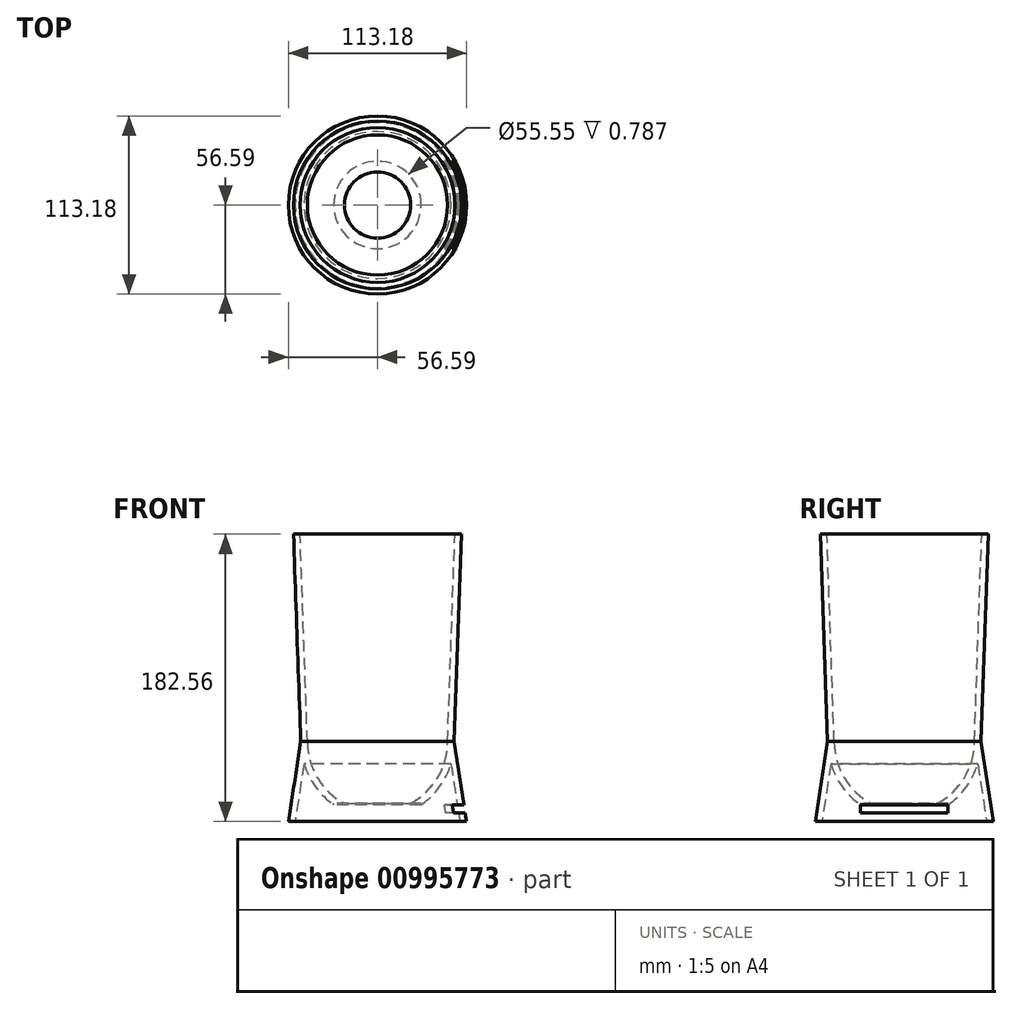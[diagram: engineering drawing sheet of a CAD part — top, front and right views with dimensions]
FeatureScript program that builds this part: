
annotation { "Feature Type Name" : "Feature", "Feature Type Description" : "" }
export const myFeature = defineFeature(function(context is Context, id is Id, definition is map)
    precondition{}
    {
        {
            var Q0;
            Q0=qCreatedBy(makeId("Front.planeOp"),FACE);
            var sketch = newSketch(context, id + "F0", { "sketchPlane" : qUnion([Q0])});
            skLineSegment(sketch, "E0", {"start": v(0, 0) * mm, "end": v(48.74, 0) * mm});
            skLineSegment(sketch, "E1", {"start": v(48.74, 0) * mm, "end": v(56.6, -50.8) * mm});
            skLineSegment(sketch, "E2", {"start": v(56.6, -50.8) * mm, "end": v(0, -50.8) * mm});
            skLineSegment(sketch, "E3", {"start": v(0, -50.8) * mm, "end": v(0, 0) * mm});
            skSolve(sketch);
        }
        {
            var Q0;
            Q0=makeQuery(id+"F0.imprint","IMPRINT",FACE,{"disambiguationData":[TD([[makeQuery(id+"F0.imprint","IMPRINT",EDGE,{"derivedFrom":sQuery(id+"F0.wireOp",EDGE,"E0")}),-1.0]])]});
            var Q1;
            Q1=sQuery(id+"F0.wireOp",EDGE,"E3");
            revolve(context, id + "F1", {"surfaceOperationType" : NewSurfaceOperationType.NEW, "entities" : qUnion([Q0]), "axis" : qUnion([Q1]), "revolveType" : RevolveType.FULL});
        }
        {
            var Q0;
            Q0=qCreatedBy(makeId("Front.planeOp"),FACE);
            var sketch = newSketch(context, id + "F2", { "sketchPlane" : qUnion([Q0])});
            skLineSegment(sketch, "E4.0", {"start": v(48.74, 0) * mm, "end": v(-48.74, 0) * mm, "construction": true});
            skLineSegment(sketch, "E5", {"start": v(0, 0) * mm, "end": v(48.74, 0) * mm});
            skLineSegment(sketch, "E6", {"start": v(0, 0) * mm, "end": v(0, 131.76) * mm});
            skLineSegment(sketch, "E7", {"start": v(0, 131.76) * mm, "end": v(53.34, 131.76) * mm});
            skLineSegment(sketch, "E8", {"start": v(53.34, 131.76) * mm, "end": v(48.74, 0) * mm});
            skSolve(sketch);
        }
        {
            var Q0;
            Q0=makeQuery(id+"F2.imprint","IMPRINT",FACE,{"disambiguationData":[TD([[makeQuery(id+"F2.imprint","IMPRINT",EDGE,{"derivedFrom":sQuery(id+"F2.wireOp",EDGE,"E5")}),1.0]])]});
            var Q1;
            Q1=sQuery(id+"F2.wireOp",EDGE,"E6");
            revolve(context, id + "F3", {"operationType" : NewBodyOperationType.ADD, "surfaceOperationType" : NewSurfaceOperationType.NEW, "entities" : qUnion([Q0]), "axis" : qUnion([Q1]), "revolveType" : RevolveType.FULL});
        }
        {
            var Q0;
            Q0=makeQuery(id+"F3.opRevolve","SWEPT_FACE",FACE,{"disambiguationData":[OSD([sQuery(id+"F2.wireOp",EDGE,"E7")])]});
            var Q1;
            Q1=makeQuery(id+"F1.opRevolve","SWEPT_FACE",FACE,{"disambiguationData":[OSD([sQuery(id+"F0.wireOp",EDGE,"E2")])]});
            shell(context, id + "F4", {"entities" : qUnion([Q0, Q1]), "thickness" : 4.2 * mm});
        }
        {
            var Q0;
            Q0=qCreatedBy(makeId("Right.planeOp"),FACE);
            var sketch = newSketch(context, id + "F5", { "sketchPlane" : qUnion([Q0])});
            skLineSegment(sketch, "E9.0", {"start": v(48.74, 0) * mm, "end": v(44.55, 0) * mm});
            skArc(sketch, "E10", {"start": v(0, -48.74) * mm, "mid": v(34.47, -34.47) * mm, "end": v(48.74, 0) * mm});
            skLineSegment(sketch, "E11", {"start": v(0, -44.55) * mm, "end": v(0, -48.74) * mm});
            skPoint(sketch, "E12.orphan", {"position": v(-48.74, 0) * mm});
            skArc(sketch, "E13", {"start": v(0, -44.55) * mm, "mid": v(31.5, -31.5) * mm, "end": v(44.55, 0) * mm});
            skSolve(sketch);
        }
        {
            var Q0;
            Q0 = qSketchRegion(id + "F5", true);
            var Q1;
            Q1=sQuery(id+"F5.wireOp",EDGE,"E11");
            revolve(context, id + "F6", {"operationType" : NewBodyOperationType.ADD, "surfaceOperationType" : NewSurfaceOperationType.NEW, "entities" : qUnion([Q0]), "axis" : qUnion([Q1]), "revolveType" : RevolveType.FULL});
        }
        {
            var Q0;
            Q0=qCreatedBy(makeId("Right.planeOp"),FACE);
            var sketch = newSketch(context, id + "F7", { "sketchPlane" : qUnion([Q0])});
            skLineSegment(sketch, "E14.0", {"start": v(27.77, -50.8) * mm, "end": v(0, -50.8) * mm});
            skLineSegment(sketch, "E15", {"start": v(0, -50.8) * mm, "end": v(0, -39.27) * mm});
            skLineSegment(sketch, "E16", {"start": v(27.77, -39.27) * mm, "end": v(27.77, -50.8) * mm});
            skLineSegment(sketch, "E17", {"start": v(27.77, -39.27) * mm, "end": v(0, -39.27) * mm});
            skPoint(sketch, "E18.orphan", {"position": v(56.6, -50.8) * mm});
            skPoint(sketch, "E19.orphan", {"position": v(-56.6, -50.8) * mm});
            skSolve(sketch);
        }
        {
            var Q0;
            Q0=makeQuery(id+"F7.imprint","IMPRINT",FACE,{"disambiguationData":[TD([[makeQuery(id+"F7.imprint","IMPRINT",EDGE,{"derivedFrom":sQuery(id+"F7.wireOp",EDGE,"E14.0")}),-1.0]])]});
            var Q1;
            Q1=sQuery(id+"F7.wireOp",EDGE,"E15");
            revolve(context, id + "F8", {"operationType" : NewBodyOperationType.REMOVE, "surfaceOperationType" : NewSurfaceOperationType.NEW, "entities" : qUnion([Q0]), "axis" : qUnion([Q1]), "revolveType" : RevolveType.FULL, "oppositeDirection" : true});
        }
        {
            var Q0;
            Q0=qCreatedBy(makeId("Right.planeOp"),FACE);
            var sketch = newSketch(context, id + "F9", { "sketchPlane" : qUnion([Q0])});
            skLineSegment(sketch, "E20.0", {"start": v(-27.77, -40.06) * mm, "end": v(27.77, -40.06) * mm});
            skLineSegment(sketch, "E21", {"start": v(-27.77, -40.06) * mm, "end": v(-27.77, -45.14) * mm});
            skLineSegment(sketch, "E22", {"start": v(-27.77, -45.14) * mm, "end": v(27.77, -45.14) * mm});
            skLineSegment(sketch, "E23", {"start": v(27.77, -45.14) * mm, "end": v(27.77, -40.06) * mm});
            skSolve(sketch);
        }
        {
            var Q0;
            Q0=makeQuery(id+"F9.imprint","IMPRINT",FACE,{"disambiguationData":[TD([[makeQuery(id+"F9.imprint","IMPRINT",EDGE,{"derivedFrom":sQuery(id+"F9.wireOp",EDGE,"E20.0")}),-1.0]])]});
            extrude(context, id + "F10", {"entities" : qUnion([Q0]), "operationType" : NewBodyOperationType.REMOVE, "endBound" : BoundingType.THROUGH_ALL, "depth" : 25.4 * mm, "offsetDistance" : 25.4 * mm});
        }
    });
